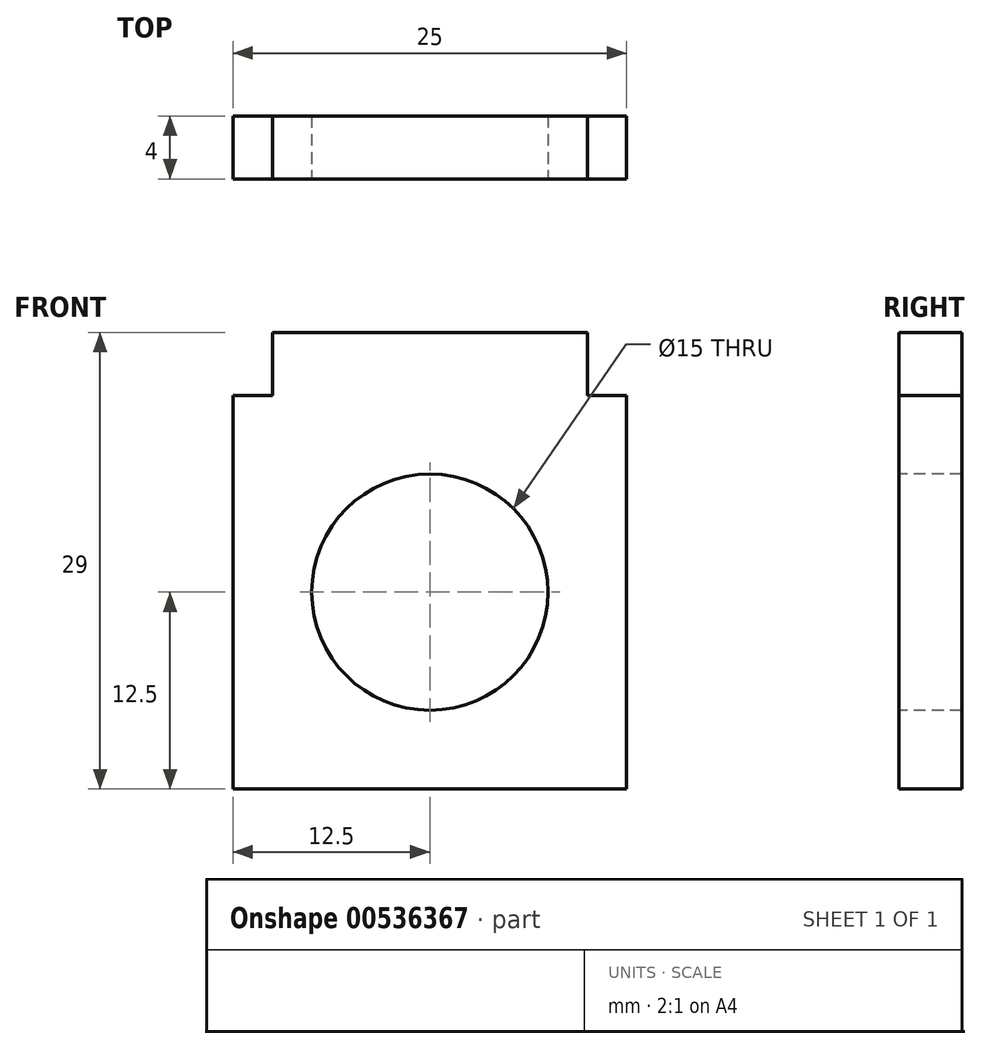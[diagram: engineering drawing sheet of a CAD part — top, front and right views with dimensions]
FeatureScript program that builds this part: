
annotation { "Feature Type Name" : "Feature", "Feature Type Description" : "" }
export const myFeature = defineFeature(function(context is Context, id is Id, definition is map)
    precondition{}
    {
        {
            var Q0;
            Q0=qCreatedBy(makeId("Front.planeOp"),FACE);
            var sketch = newSketch(context, id + "F0", { "sketchPlane" : qUnion([Q0])});
            skLineSegment(sketch, "E0.bottom", {"start": v(-12.5, -12.5) * mm, "end": v(12.5, -12.5) * mm});
            skLineSegment(sketch, "E0.top", {"start": v(-12.5, 12.5) * mm, "end": v(12.5, 12.5) * mm});
            skLineSegment(sketch, "E0.left", {"start": v(-12.5, -12.5) * mm, "end": v(-12.5, 12.5) * mm});
            skLineSegment(sketch, "E0.right", {"start": v(12.5, -12.5) * mm, "end": v(12.5, 12.5) * mm});
            skPoint(sketch, "E0.middle", {"position": v(0, 0) * mm});
            skLineSegment(sketch, "E1", {"start": v(0, 12.5) * mm, "end": v(0, 16.5) * mm});
            skPoint(sketch, "E1.endSnap0", {"position": v(0, 12.5) * mm});
            skLineSegment(sketch, "E2", {"start": v(0, 16.5) * mm, "end": v(-10, 16.5) * mm});
            skLineSegment(sketch, "E3", {"start": v(-10, 16.5) * mm, "end": v(-10, 12.5) * mm});
            skLineSegment(sketch, "E4", {"start": v(-10, 12.5) * mm, "end": v(0, 12.5) * mm});
            skLineSegment(sketch, "E5", {"start": v(0, 16.5) * mm, "end": v(10, 16.5) * mm});
            skLineSegment(sketch, "E6", {"start": v(10, 16.5) * mm, "end": v(10, 12.5) * mm});
            skLineSegment(sketch, "E7", {"start": v(10, 12.5) * mm, "end": v(0, 12.5) * mm});
            skSolve(sketch);
        }
        {
            var Q0;
            Q0=makeQuery(id+"F0.imprint","IMPRINT",FACE,{"disambiguationData":[TD([[makeQuery(id+"F0.imprint","IMPRINT",EDGE,{"derivedFrom":sQuery(id+"F0.wireOp",EDGE,"E0.bottom")}),1.0]])]});
            var Q1;
            Q1=makeQuery(id+"F0.imprint","IMPRINT",FACE,{"disambiguationData":[TD([[makeQuery(id+"F0.imprint","IMPRINT",EDGE,{"derivedFrom":sQuery(id+"F0.wireOp",EDGE,"E1")}),1.0]])]});
            var Q2;
            Q2=makeQuery(id+"F0.imprint","IMPRINT",FACE,{"disambiguationData":[TD([[makeQuery(id+"F0.imprint","IMPRINT",EDGE,{"derivedFrom":sQuery(id+"F0.wireOp",EDGE,"E1")}),-1.0]])]});
            extrude(context, id + "F1", {"entities" : qUnion([Q0, Q1, Q2]), "depth" : 4 * mm, "offsetDistance" : 25 * mm});
        }
        {
            var Q0;
            Q0=makeQuery(id+"F1.opExtrude","CAP_FACE",FACE,{"disambiguationData":[OSD([sQuery(id+"F0.wireOp",EDGE,"E0.bottom"),sQuery(id+"F0.wireOp",EDGE,"E0.top"),sQuery(id+"F0.wireOp",EDGE,"E0.left"),sQuery(id+"F0.wireOp",EDGE,"E0.right"),sQuery(id+"F0.wireOp",EDGE,"E2"),sQuery(id+"F0.wireOp",EDGE,"E3"),sQuery(id+"F0.wireOp",EDGE,"E5"),sQuery(id+"F0.wireOp",EDGE,"E6")])],"isStart":false});
            var sketch = newSketch(context, id + "F2", { "sketchPlane" : qUnion([Q0])});
            skLineSegment(sketch, "E8", {"start": v(12.5, 0) * mm, "end": v(-12.5, 0) * mm});
            skCircle(sketch, "E9", {"center": v(0, 0) * mm, "radius": 7.5 * mm});
            skSolve(sketch);
        }
        {
            var Q0;
            {var subQ0=sQuery(id+"F2.wireOp",EDGE,"E9");var subQ1=sQuery(id+"F2.wireOp",EDGE,"E8");var subQ2=makeQuery(id+"F2.imprint","INTERSECT",VERTEX,{"disambiguationData":[OD(0.0)],"derivedFrom":[subQ1,subQ0]});Q0=makeQuery(id+"F2.imprint","IMPRINT",FACE,{"disambiguationData":[TD([[makeQuery(id+"F2.imprint","IMPRINT",EDGE,{"disambiguationData":[TD([[subQ2,-1.0]])],"derivedFrom":subQ1}),-1.0]])]});}
            var Q1;
            {var subQ0=sQuery(id+"F2.wireOp",EDGE,"E9");var subQ1=sQuery(id+"F2.wireOp",EDGE,"E8");var subQ2=makeQuery(id+"F2.imprint","INTERSECT",VERTEX,{"disambiguationData":[OD(0.0)],"derivedFrom":[subQ1,subQ0]});Q1=makeQuery(id+"F2.imprint","IMPRINT",FACE,{"disambiguationData":[TD([[makeQuery(id+"F2.imprint","IMPRINT",EDGE,{"disambiguationData":[TD([[subQ2,-1.0]])],"derivedFrom":subQ1}),1.0]])]});}
            extrude(context, id + "F3", {"entities" : qUnion([Q0, Q1]), "operationType" : NewBodyOperationType.REMOVE, "oppositeDirection" : true, "depth" : 25 * mm, "offsetDistance" : 25 * mm});
        }
    });
